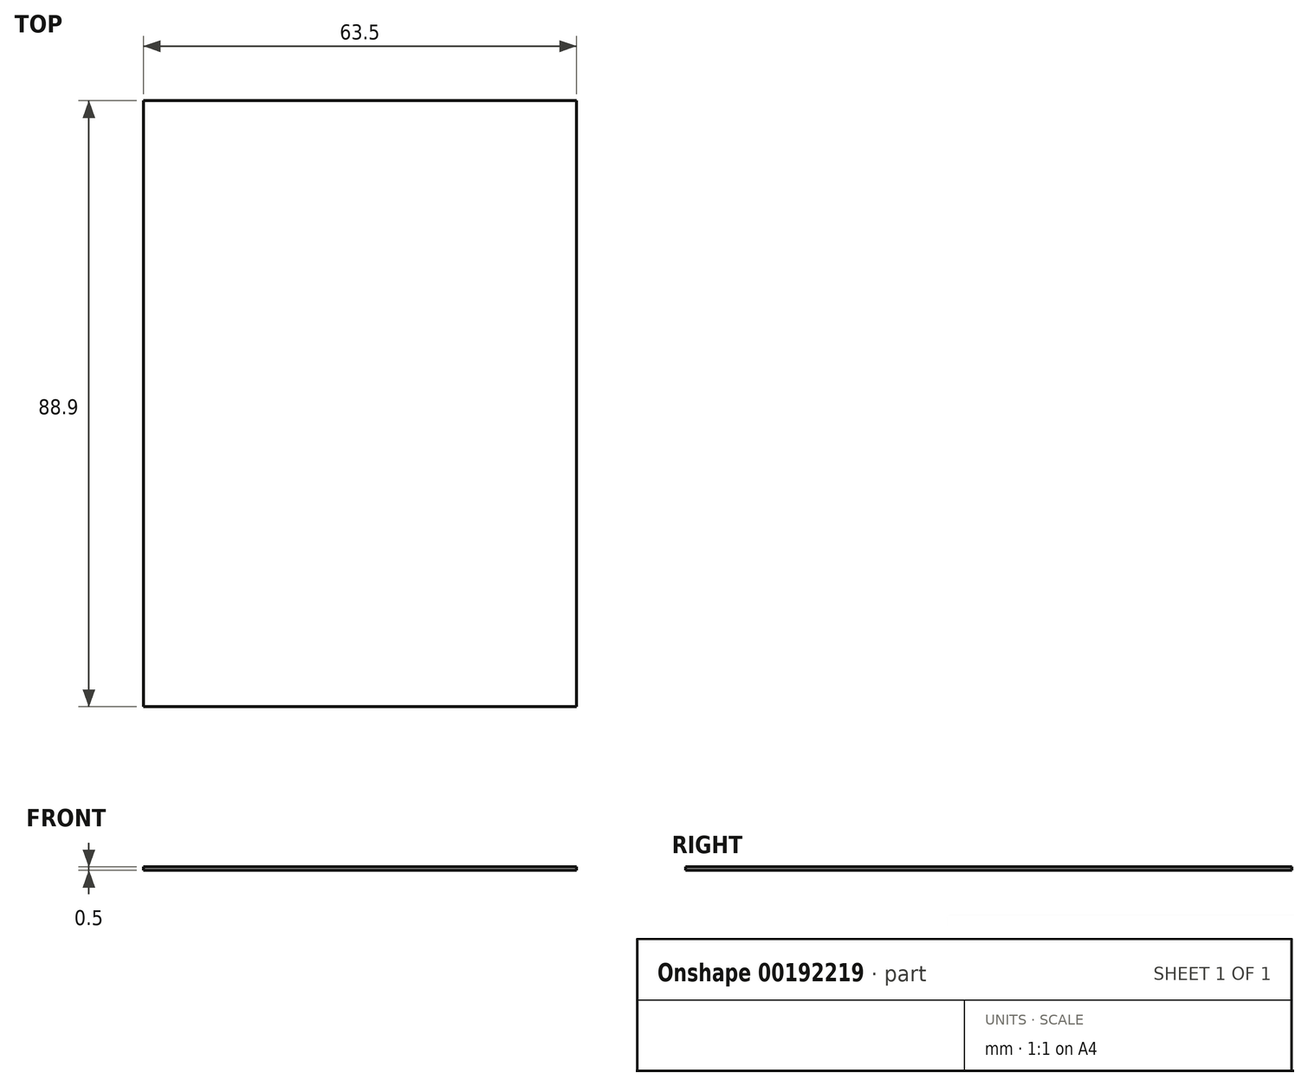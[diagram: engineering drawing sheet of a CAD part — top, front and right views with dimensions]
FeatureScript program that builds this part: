
annotation { "Feature Type Name" : "Feature", "Feature Type Description" : "" }
export const myFeature = defineFeature(function(context is Context, id is Id, definition is map)
    precondition{}
    {
        {
            var Q0;
            Q0=qCreatedBy(makeId("Top.planeOp"),FACE);
            var sketch = newSketch(context, id + "F0", { "sketchPlane" : qUnion([Q0])});
            skLineSegment(sketch, "E0.bottom", {"start": v(31.75, 44.45) * mm, "end": v(-31.75, 44.45) * mm});
            skLineSegment(sketch, "E0.top", {"start": v(31.75, -44.45) * mm, "end": v(-31.75, -44.45) * mm});
            skLineSegment(sketch, "E0.left", {"start": v(31.75, 44.45) * mm, "end": v(31.75, -44.45) * mm});
            skLineSegment(sketch, "E0.right", {"start": v(-31.75, 44.45) * mm, "end": v(-31.75, -44.45) * mm});
            skPoint(sketch, "E0.middle", {"position": v(0, 0) * mm});
            skSolve(sketch);
        }
        {
            var Q0;
            Q0=makeQuery(id+"F0.imprint","IMPRINT",FACE,{"disambiguationData":[TD([[makeQuery(id+"F0.imprint","IMPRINT",EDGE,{"derivedFrom":sQuery(id+"F0.wireOp",EDGE,"E0.bottom")}),1.0]])]});
            extrude(context, id + "F1", {"entities" : qUnion([Q0]), "depth" : .5 * mm});
        }
    });
